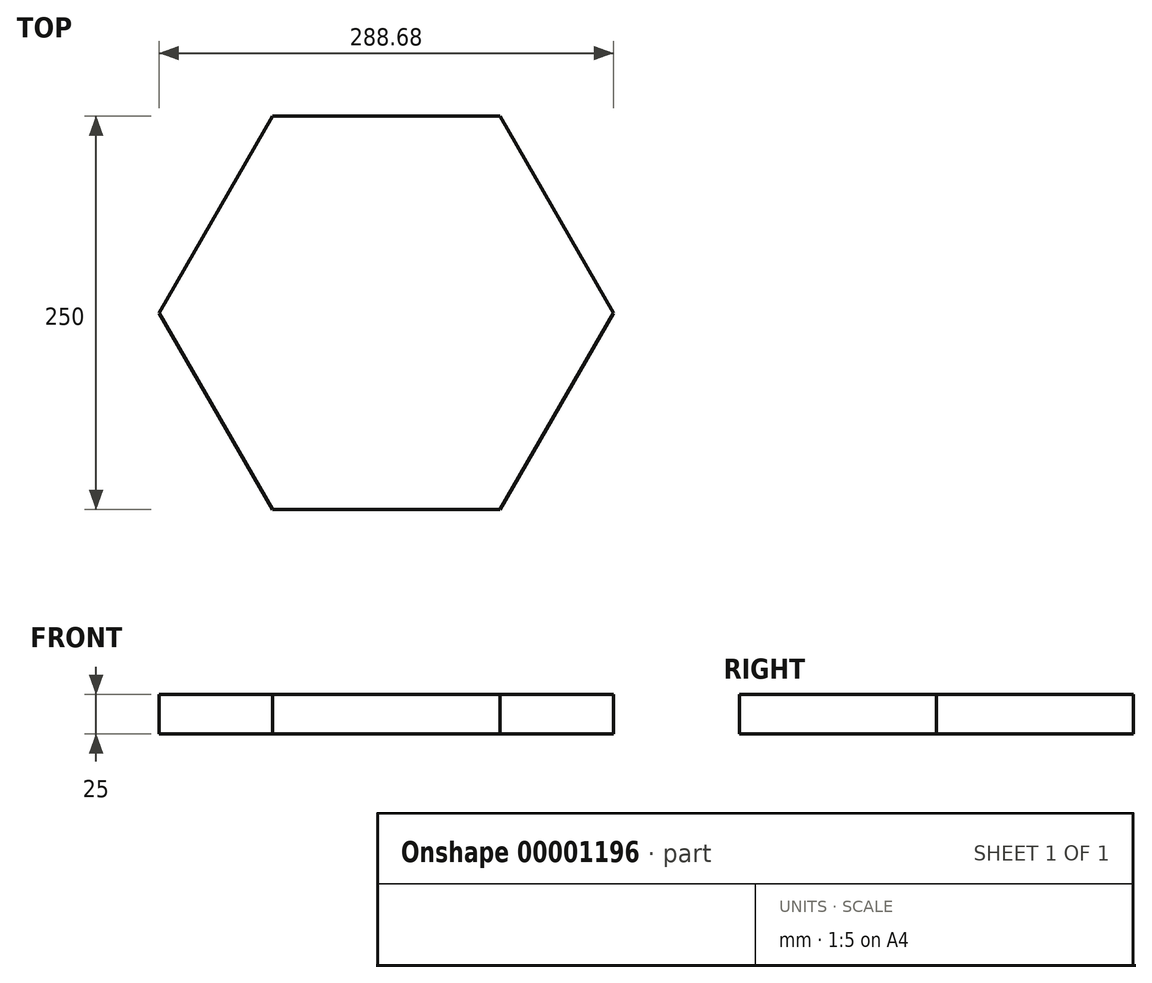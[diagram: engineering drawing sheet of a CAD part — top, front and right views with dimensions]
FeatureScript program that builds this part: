
annotation { "Feature Type Name" : "Feature", "Feature Type Description" : "" }
export const myFeature = defineFeature(function(context is Context, id is Id, definition is map)
    precondition{}
    {
        {
            var Q0;
            Q0=qCreatedBy(makeId("Top.planeOp"),FACE);
            var sketch = newSketch(context, id + "F0", { "sketchPlane" : qUnion([Q0])});
            skCircle(sketch, "E0.cCircle", {"center": v(78.33, 14.71) * mm, "radius": 125 * mm, "construction": true});
            skLineSegment(sketch, "E0.0", {"start": v(6.16, -110.29) * mm, "end": v(-66, 14.71) * mm});
            skLineSegment(sketch, "E0.1", {"start": v(-66, 14.71) * mm, "end": v(6.16, 139.71) * mm});
            skLineSegment(sketch, "E0.2", {"start": v(6.16, 139.71) * mm, "end": v(150.5, 139.71) * mm});
            skLineSegment(sketch, "E0.3", {"start": v(150.5, 139.71) * mm, "end": v(222.67, 14.71) * mm});
            skLineSegment(sketch, "E0.4", {"start": v(222.67, 14.71) * mm, "end": v(150.5, -110.29) * mm});
            skLineSegment(sketch, "E0.5", {"start": v(150.5, -110.29) * mm, "end": v(6.16, -110.29) * mm});
            skPoint(sketch, "E0.0.midPoint", {"position": v(-29.92, -47.79) * mm});
            skSolve(sketch);
        }
        {
            var Q0;
            Q0 = qSketchRegion(id + "F0", true);
            extrude(context, id + "F1", {"entities" : qUnion([Q0]), "depth" : 25 * mm});
        }
        {
            var Q0;
            Q0=makeQuery(id+"F1.opExtrude","SWEPT_BODY",BODY,{"disambiguationData":[OSD([sQuery(id+"F0.wireOp",EDGE,"E0.0"),sQuery(id+"F0.wireOp",EDGE,"E0.1"),sQuery(id+"F0.wireOp",EDGE,"E0.2"),sQuery(id+"F0.wireOp",EDGE,"E0.3"),sQuery(id+"F0.wireOp",EDGE,"E0.4"),sQuery(id+"F0.wireOp",EDGE,"E0.5")])]});
            var Q1;
            Q1=sQuery(id+"F0.wireOp",VERTEX,"E0.cCircle.center");
            var Q2;
            Q2=qCreatedBy(makeId("Origin.pointOp"),VERTEX);
            transform(context, id + "F2", {"entities" : qUnion([Q0]), "transformType" : TransformType.TRANSLATION_ENTITY, "oppositeDirectionEntity" : false, "transformLine" : qUnion([Q1, Q2]), "makeCopy" : false});
        }
    });
